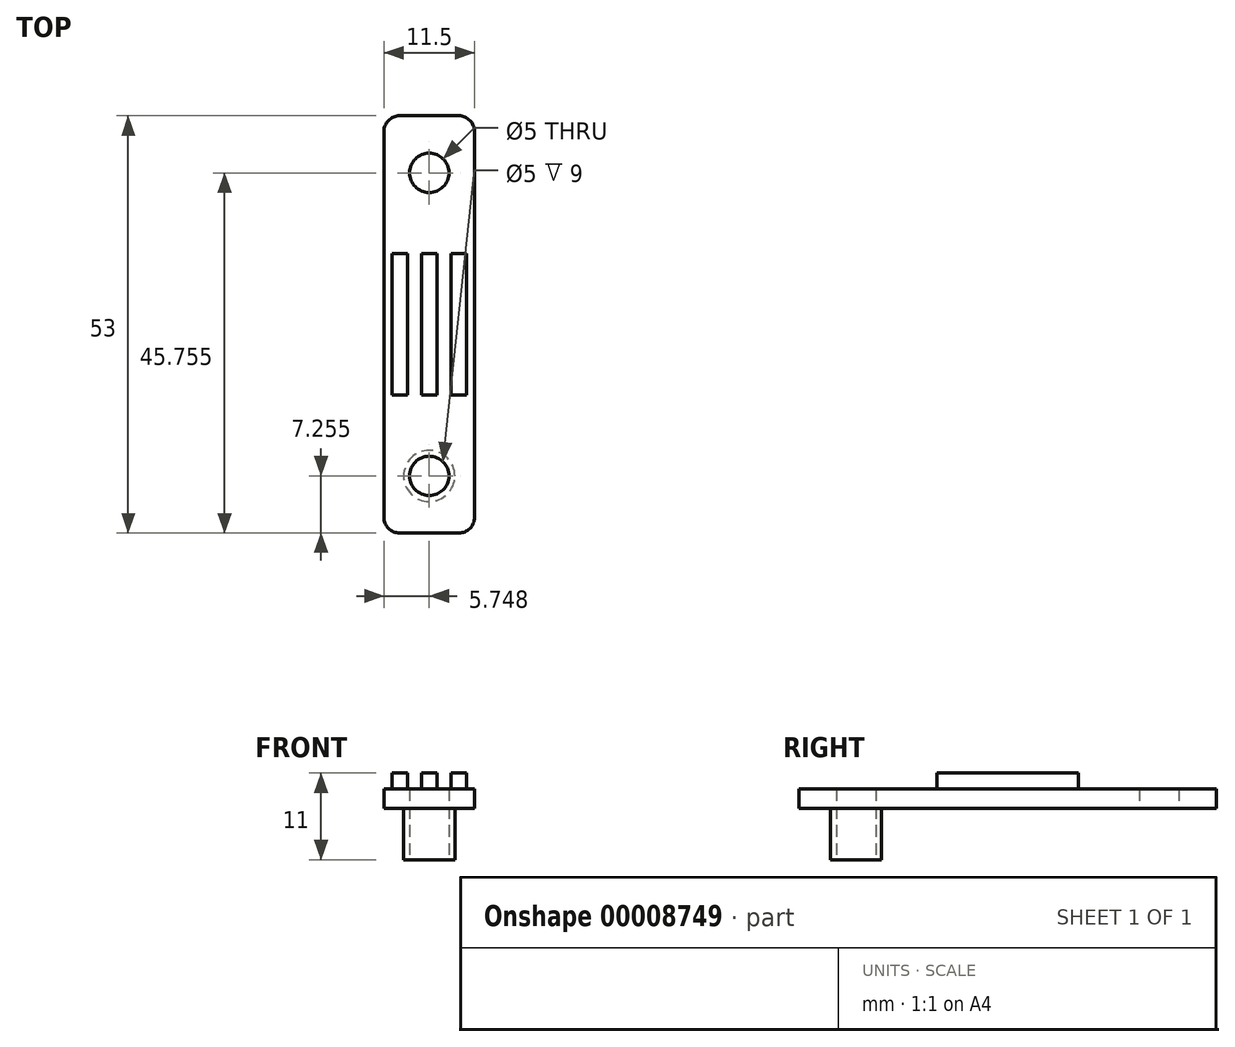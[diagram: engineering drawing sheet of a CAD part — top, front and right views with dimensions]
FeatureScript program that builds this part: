
annotation { "Feature Type Name" : "Feature", "Feature Type Description" : "" }
export const myFeature = defineFeature(function(context is Context, id is Id, definition is map)
    precondition{}
    {
        {
            var Q0;
            Q0=qCreatedBy(makeId("Top.planeOp"),FACE);
            var sketch = newSketch(context, id + "F0", { "sketchPlane" : qUnion([Q0])});
            skLineSegment(sketch, "E0.bottom", {"start": v(-14.8, 31.1) * mm, "end": v(-3.3, 31.1) * mm});
            skLineSegment(sketch, "E0.top", {"start": v(-14.8, -21.9) * mm, "end": v(-3.3, -21.9) * mm});
            skLineSegment(sketch, "E0.left", {"start": v(-14.8, 31.1) * mm, "end": v(-14.8, -21.9) * mm});
            skLineSegment(sketch, "E0.right", {"start": v(-3.3, 31.1) * mm, "end": v(-3.3, -21.9) * mm});
            skPoint(sketch, "E1", {"position": v(-9.05, 31.1) * mm});
            skLineSegment(sketch, "E2", {"start": v(-9.05, 31.1) * mm, "end": v(-9.05, -21.9) * mm, "construction": true});
            skCircle(sketch, "E3", {"center": v(-9.05, 23.84) * mm, "radius": 2.5 * mm});
            skLineSegment(sketch, "E4", {"start": v(-14.8, 4.6) * mm, "end": v(-3.3, 4.6) * mm, "construction": true});
            skCircle(sketch, "E5.0.MirrorC", {"center": v(-9.05, -14.66) * mm, "radius": 2.5 * mm});
            skSolve(sketch);
        }
        {
            var Q0;
            Q0=makeQuery(id+"F0.imprint","IMPRINT",FACE,{"disambiguationData":[TD([[makeQuery(id+"F0.imprint","IMPRINT",EDGE,{"derivedFrom":sQuery(id+"F0.wireOp",EDGE,"E0.bottom")}),-1.0]])]});
            extrude(context, id + "F1", {"entities" : qUnion([Q0]), "depth" : 9 * mm});
        }
        {
            var Q0;
            Q0=makeQuery(id+"F1.opExtrude","CAP_FACE",FACE,{"disambiguationData":[OSD([sQuery(id+"F0.wireOp",EDGE,"E0.bottom"),sQuery(id+"F0.wireOp",EDGE,"E0.top"),sQuery(id+"F0.wireOp",EDGE,"E0.left"),sQuery(id+"F0.wireOp",EDGE,"E0.right"),sQuery(id+"F0.wireOp",EDGE,"E3"),sQuery(id+"F0.wireOp",EDGE,"64c8e85a-237b-4d90-a55e-2ac8bd8c3d32")])],"isStart":true});
            var sketch = newSketch(context, id + "F2", { "sketchPlane" : qUnion([Q0])});
            skCircle(sketch, "E6.0", {"center": v(-9.05, -23.84) * mm, "radius": 2.5 * mm, "construction": true});
            skCircle(sketch, "E7", {"center": v(-9.05, -23.84) * mm, "radius": 3.25 * mm});
            skCircle(sketch, "E8.0", {"center": v(-9.05, 14.66) * mm, "radius": 2.5 * mm, "construction": true});
            skLineSegment(sketch, "E9", {"start": v(-14.8, -4.6) * mm, "end": v(-3.3, -4.6) * mm, "construction": true});
            skCircle(sketch, "E10.0.MirrorC", {"center": v(-9.05, 14.66) * mm, "radius": 3.25 * mm});
            skSolve(sketch);
        }
        {
            var Q0;
            Q0=makeQuery(id+"F2.imprint","IMPRINT",FACE,{"disambiguationData":[TD([[makeQuery(id+"F2.imprint","IMPRINT",EDGE,{"derivedFrom":sQuery(id+"F2.wireOp",EDGE,"E7")}),1.0]])]});
            var Q1;
            Q1=makeQuery(id+"F2.imprint","IMPRINT",FACE,{"disambiguationData":[TD([[makeQuery(id+"F2.imprint","IMPRINT",EDGE,{"derivedFrom":sQuery(id+"F2.wireOp",EDGE,"E10.0.MirrorC")}),-1.0]])]});
            extrude(context, id + "F3", {"entities" : qUnion([Q0, Q1]), "operationType" : NewBodyOperationType.REMOVE, "oppositeDirection" : true, "depth" : 6.5 * mm});
        }
        {
            var Q0;
            Q0=makeQuery(id+"F1.opExtrude","CAP_FACE",FACE,{"disambiguationData":[OSD([sQuery(id+"F0.wireOp",EDGE,"E0.bottom"),sQuery(id+"F0.wireOp",EDGE,"E0.top"),sQuery(id+"F0.wireOp",EDGE,"E0.left"),sQuery(id+"F0.wireOp",EDGE,"E0.right"),sQuery(id+"F0.wireOp",EDGE,"E3"),sQuery(id+"F0.wireOp",EDGE,"64c8e85a-237b-4d90-a55e-2ac8bd8c3d32")])],"isStart":false});
            var sketch = newSketch(context, id + "F4", { "sketchPlane" : qUnion([Q0])});
            skLineSegment(sketch, "E11", {"start": v(-14.8, 4.6) * mm, "end": v(-3.3, 4.6) * mm, "construction": true});
            skLineSegment(sketch, "E12.top", {"start": v(-14.8, -4.4) * mm, "end": v(-3.3, -4.4) * mm});
            skLineSegment(sketch, "E12.left", {"start": v(-14.8, 4.6) * mm, "end": v(-14.8, -4.4) * mm});
            skLineSegment(sketch, "E12.right", {"start": v(-3.3, 4.6) * mm, "end": v(-3.3, -4.4) * mm});
            skLineSegment(sketch, "E13.0.MirrorCS", {"start": v(-14.8, 13.6) * mm, "end": v(-3.3, 13.6) * mm});
            skLineSegment(sketch, "E14.0.MirrorCS", {"start": v(-14.8, 4.6) * mm, "end": v(-14.8, 13.6) * mm});
            skLineSegment(sketch, "E15.0.MirrorCS", {"start": v(-3.3, 4.6) * mm, "end": v(-3.3, 13.6) * mm});
            skLineSegment(sketch, "E16", {"start": v(-9.05, 31.1) * mm, "end": v(-9.05, -21.9) * mm, "construction": true});
            skLineSegment(sketch, "E17", {"start": v(-11.8, 13.6) * mm, "end": v(-11.8, -4.4) * mm});
            skLineSegment(sketch, "E18.0.MirrorCS", {"start": v(-6.3, 13.6) * mm, "end": v(-6.3, -4.4) * mm});
            skLineSegment(sketch, "E19", {"start": v(-13.8, 13.6) * mm, "end": v(-13.8, -4.4) * mm});
            skLineSegment(sketch, "E20.0.MirrorCS", {"start": v(-4.3, 13.6) * mm, "end": v(-4.3, -4.4) * mm});
            skLineSegment(sketch, "E21", {"start": v(-10.05, 13.6) * mm, "end": v(-10.05, -4.4) * mm});
            skLineSegment(sketch, "E22.0.MirrorCS", {"start": v(-8.05, 13.6) * mm, "end": v(-8.05, -4.4) * mm});
            skSolve(sketch);
        }
        {
            var Q0;
            {var subQ1=sQuery(id+"F4.wireOp",EDGE,"E17");Q0=makeQuery(id+"F4.imprint","IMPRINT",FACE,{"disambiguationData":[TD([[makeQuery(id+"F4.imprint","IMPRINT",EDGE,{"derivedFrom":subQ1}),-1.0]])]});}
            var Q1;
            {var subQ1=sQuery(id+"F4.wireOp",EDGE,"E18.0.MirrorCS");Q1=makeQuery(id+"F4.imprint","IMPRINT",FACE,{"disambiguationData":[TD([[makeQuery(id+"F4.imprint","IMPRINT",EDGE,{"derivedFrom":subQ1}),1.0]])]});}
            var Q2;
            {var subQ1=sQuery(id+"F4.wireOp",EDGE,"E21");Q2=makeQuery(id+"F4.imprint","IMPRINT",FACE,{"disambiguationData":[TD([[makeQuery(id+"F4.imprint","IMPRINT",EDGE,{"derivedFrom":subQ1}),1.0]])]});}
            extrude(context, id + "F5", {"entities" : qUnion([Q0, Q1, Q2]), "operationType" : NewBodyOperationType.ADD, "depth" : 2 * mm});
        }
        {
            var Q0;
            Q0=makeQuery(id+"F1.opExtrude","SWEPT_EDGE",EDGE,{"disambiguationData":[OSD([sQuery(id+"F0.wireOp",EDGE,"E0.bottom"),sQuery(id+"F0.wireOp",EDGE,"E0.left")])]});
            var Q1;
            Q1=makeQuery(id+"F1.opExtrude","SWEPT_EDGE",EDGE,{"disambiguationData":[OSD([sQuery(id+"F0.wireOp",EDGE,"E0.top"),sQuery(id+"F0.wireOp",EDGE,"E0.left")])]});
            var Q2;
            Q2=makeQuery(id+"F1.opExtrude","SWEPT_EDGE",EDGE,{"disambiguationData":[OSD([sQuery(id+"F0.wireOp",EDGE,"E0.top"),sQuery(id+"F0.wireOp",EDGE,"E0.right")])]});
            var Q3;
            Q3=makeQuery(id+"F1.opExtrude","SWEPT_EDGE",EDGE,{"disambiguationData":[OSD([sQuery(id+"F0.wireOp",EDGE,"E0.bottom"),sQuery(id+"F0.wireOp",EDGE,"E0.right")])]});
            fillet(context, id + "F6", {"entities" : qUnion([Q0, Q1, Q2, Q3]), "radius" : 2 * mm, "tangentPropagation" : true, "allowEdgeOverflow" : false});
        }
    });
